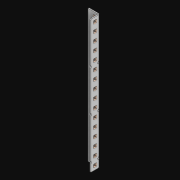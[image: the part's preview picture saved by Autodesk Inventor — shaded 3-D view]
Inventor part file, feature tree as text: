
AUTODESK INVENTOR PART (.ipt)
format: ipt  version: 2021 (Build 250183000, 183)  size: 1,174,528 bytes
history: native  units: in
note: dims shown in document units (in); Inventor stores cm internally (conversion verified against a paired STEP export)
features: extrude x34, other x32, sketch x4, pattern_linear x2, sheet_metal_op x1
ambient origin geometry x8: Origin, YZ Plane, XZ Plane, XY Plane, X Axis, Y Axis, Z Axis, Center Point
bodies: Solid1 (feature_tree)
feature tree (73):
  pattern_linear  "Rectangular Pattern1"  Spacing1=0.5in  [1 undecoded]
  pattern_linear  "Rectangular Pattern3"  Count1=16  [1 undecoded]
  extrude  "Extrusion1"  Depth=0.5in
  extrude  "Extrusion2"  Depth=0.5in
  sketch  "Sketch1"  dims[d0=0.182in]
  other  "Srf1"
  sketch  "Sketch3"  dims[d1=0.063in d2=0.0in]
  other  "Srf3"
  other  "Srf4"
  other  "Srf5"
  other  "Srf6"
  other  "Srf7"
  other  "Srf8"
  other  "Srf9"
  other  "Srf10"
  other  "Srf11"
  other  "Srf12"
  other  "Srf13"
  other  "Srf14"
  other  "Srf15"
  other  "Srf16"
  other  "Srf17"
  other  "Srf18"
  other  "Srf142"
  other  "Srf143"
  other  "Srf144"
  other  "Srf145"
  other  "Srf146"
  other  "Srf147"
  other  "Srf148"
  other  "Srf149"
  other  "Srf150"
  other  "Srf151"
  other  "Srf152"
  other  "Srf153"
  other  "Srf154"
  other  "Srf155"
  other  "Srf156"
  sketch  "Sketch4"  dims[d6=0.182in]
  sketch  "Sketch5"  dims[d7=0.063in d8=0.0in d11=0.5in d12=0.3937in d14=0.5in d18=6.2992in d20=0.5in d21=9.5in d22=0.0in d23=0.841in d24=0.0in]
  sheet_metal_op  "Fold1"
  extrude  "ExtrusionSrf1"  TaperAngle=0.0deg  [1 undecoded]
  extrude  "ExtrusionSrf3"  Depth=0.5in TaperAngle=0.0deg
  extrude  "ExtrusionSrf4"  [1 undecoded]
  extrude  "ExtrusionSrf5"  [1 undecoded]
  extrude  "ExtrusionSrf6"  [1 undecoded]
  extrude  "ExtrusionSrf7"  [1 undecoded]
  extrude  "ExtrusionSrf8"  [1 undecoded]
  extrude  "ExtrusionSrf9"  [1 undecoded]
  extrude  "ExtrusionSrf10"  [1 undecoded]
  extrude  "ExtrusionSrf11"  [1 undecoded]
  extrude  "ExtrusionSrf12"  [1 undecoded]
  extrude  "ExtrusionSrf13"  [1 undecoded]
  extrude  "ExtrusionSrf14"  [1 undecoded]
  extrude  "ExtrusionSrf15"  [1 undecoded]
  extrude  "ExtrusionSrf16"  [1 undecoded]
  extrude  "ExtrusionSrf17"  [1 undecoded]
  extrude  "ExtrusionSrf18"  [1 undecoded]
  extrude  "ExtrusionSrf142"  [1 undecoded]
  extrude  "ExtrusionSrf143"  [1 undecoded]
  extrude  "ExtrusionSrf144"  [1 undecoded]
  extrude  "ExtrusionSrf145"  [1 undecoded]
  extrude  "ExtrusionSrf146"  [1 undecoded]
  extrude  "ExtrusionSrf147"  [1 undecoded]
  extrude  "ExtrusionSrf148"  [1 undecoded]
  extrude  "ExtrusionSrf149"  [1 undecoded]
  extrude  "ExtrusionSrf150"  [1 undecoded]
  extrude  "ExtrusionSrf151"  [1 undecoded]
  extrude  "ExtrusionSrf152"  [1 undecoded]
  extrude  "ExtrusionSrf153"  [1 undecoded]
  extrude  "ExtrusionSrf154"  [1 undecoded]
  extrude  "ExtrusionSrf155"  [1 undecoded]
  extrude  "ExtrusionSrf156"  [1 undecoded]
note: 33 required parameter values undecoded (feature->parameter linkage not recoverable at this tier; creation-order binding heuristic only, values carry confidence <= 0.55)
